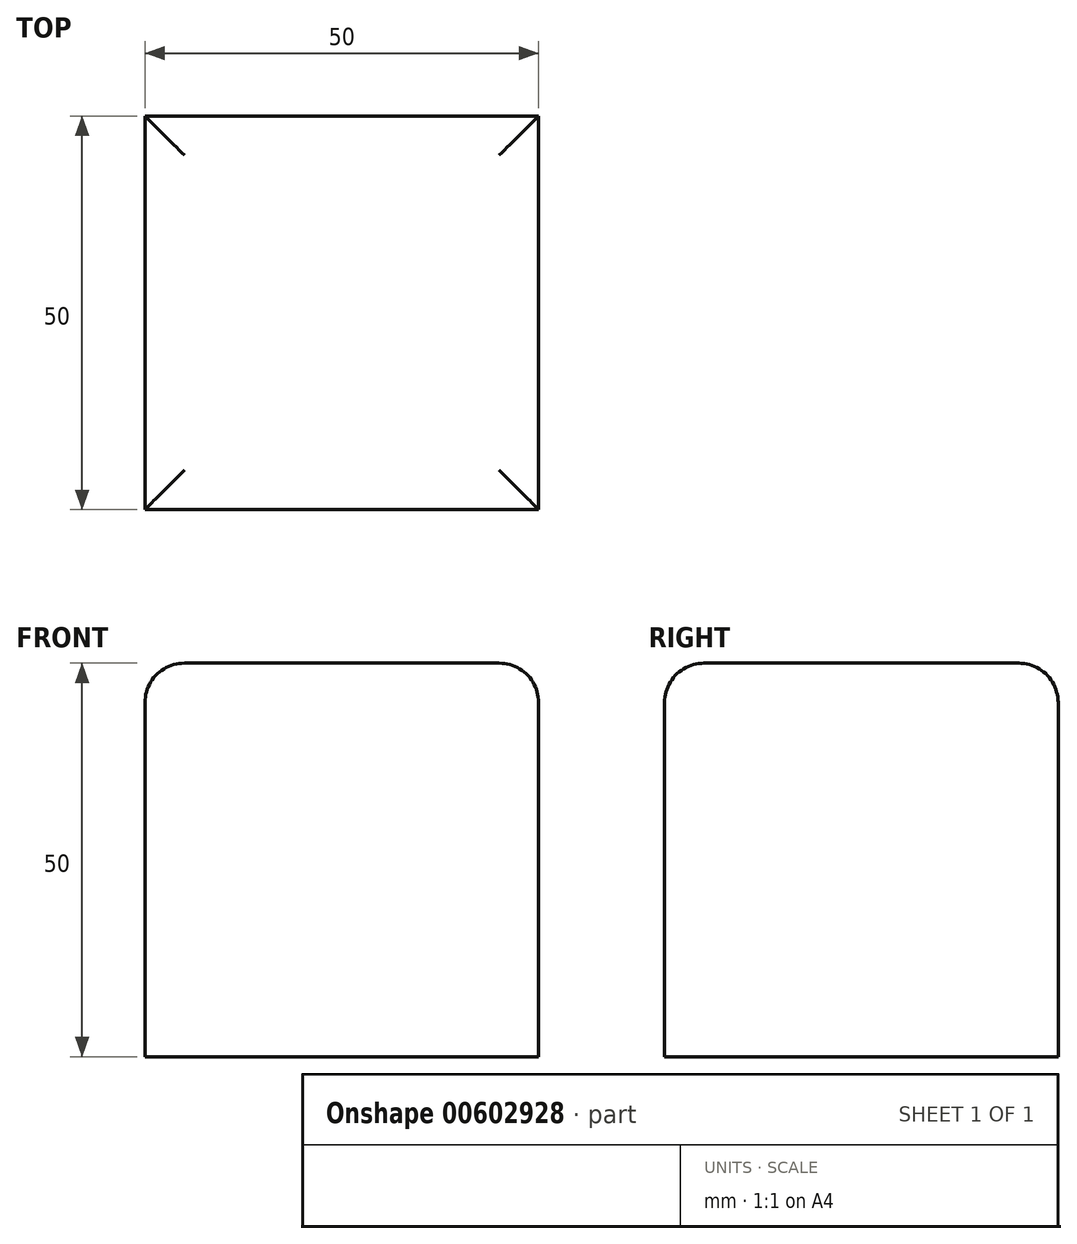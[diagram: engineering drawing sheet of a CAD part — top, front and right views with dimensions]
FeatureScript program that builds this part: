
annotation { "Feature Type Name" : "Feature", "Feature Type Description" : "" }
export const myFeature = defineFeature(function(context is Context, id is Id, definition is map)
    precondition{}
    {
        {
            var Q0;
            Q0=qCreatedBy(makeId("Top.planeOp"),FACE);
            var sketch = newSketch(context, id + "F0", { "sketchPlane" : qUnion([Q0])});
            skLineSegment(sketch, "E0.bottom", {"start": v(0, 0) * mm, "end": v(50, 0) * mm});
            skLineSegment(sketch, "E0.top", {"start": v(0, 50) * mm, "end": v(50, 50) * mm});
            skLineSegment(sketch, "E0.left", {"start": v(0, 0) * mm, "end": v(0, 50) * mm});
            skLineSegment(sketch, "E0.right", {"start": v(50, 0) * mm, "end": v(50, 50) * mm});
            skSolve(sketch);
        }
        {
            var Q0;
            Q0=makeQuery(id+"F0.imprint","IMPRINT",FACE,{"disambiguationData":[TD([[makeQuery(id+"F0.imprint","IMPRINT",EDGE,{"derivedFrom":sQuery(id+"F0.wireOp",EDGE,"E0.bottom")}),1.0]])]});
            extrude(context, id + "F1", {"entities" : qUnion([Q0]), "depth" : 50 * mm, "offsetDistance" : 25 * mm});
        }
        {
            var Q0;
            Q0=makeQuery(id+"F1.opExtrude","CAP_EDGE",EDGE,{"disambiguationData":[OSD([sQuery(id+"F0.wireOp",EDGE,"E0.top")])],"isStart":false});
            var Q1;
            Q1=makeQuery(id+"F1.opExtrude","CAP_EDGE",EDGE,{"disambiguationData":[OSD([sQuery(id+"F0.wireOp",EDGE,"E0.right")])],"isStart":false});
            var Q2;
            Q2=makeQuery(id+"F1.opExtrude","CAP_EDGE",EDGE,{"disambiguationData":[OSD([sQuery(id+"F0.wireOp",EDGE,"E0.bottom")])],"isStart":false});
            var Q3;
            Q3=makeQuery(id+"F1.opExtrude","CAP_EDGE",EDGE,{"disambiguationData":[OSD([sQuery(id+"F0.wireOp",EDGE,"E0.left")])],"isStart":false});
            fillet(context, id + "F2", {"entities" : qUnion([Q0, Q1, Q2, Q3]), "radius" : 5 * mm, "tangentPropagation" : true, "allowEdgeOverflow" : false});
        }
    });
